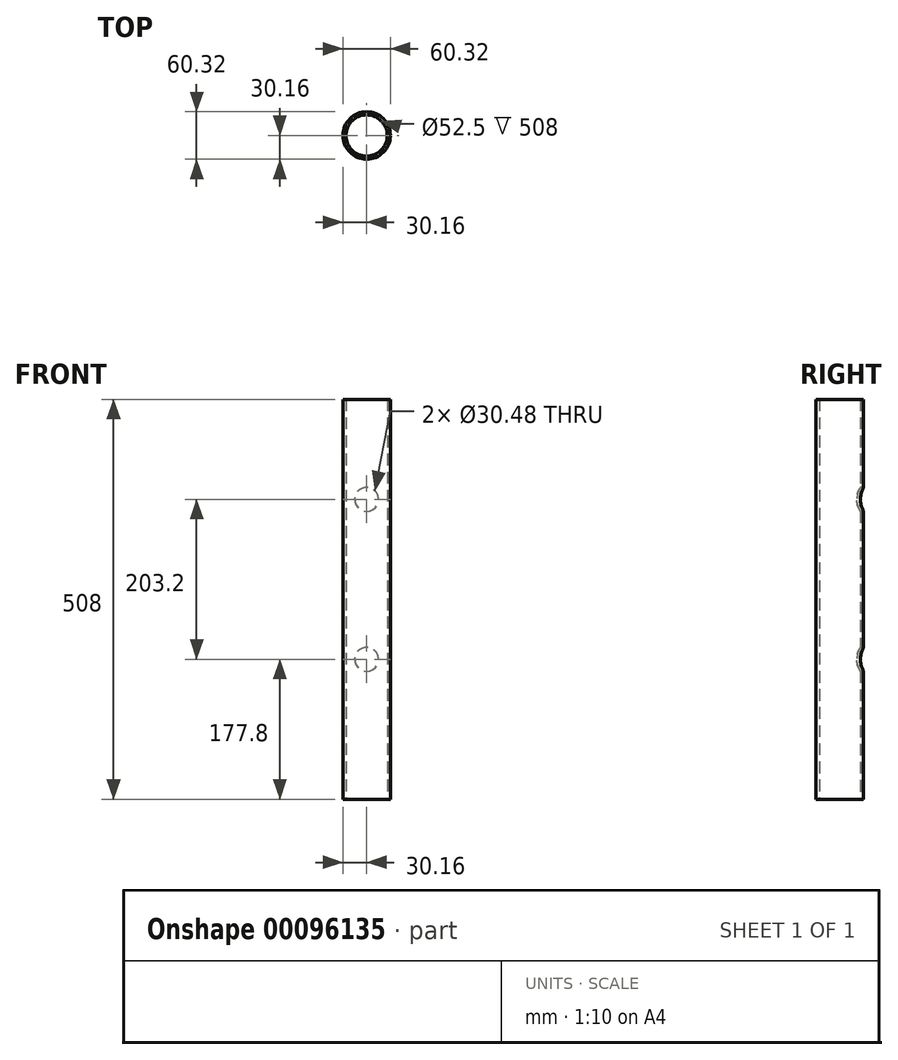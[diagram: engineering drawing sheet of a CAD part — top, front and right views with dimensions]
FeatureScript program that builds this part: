
annotation { "Feature Type Name" : "Feature", "Feature Type Description" : "" }
export const myFeature = defineFeature(function(context is Context, id is Id, definition is map)
    precondition{}
    {
        {
            var Q0;
            Q0=qCreatedBy(makeId("Top.planeOp"),FACE);
            var sketch = newSketch(context, id + "F0", { "sketchPlane" : qUnion([Q0])});
            skCircle(sketch, "E0", {"center": v(0, 0) * mm, "radius": 26.25 * mm});
            skCircle(sketch, "E1", {"center": v(0, 0) * mm, "radius": 30.16 * mm});
            skSolve(sketch);
        }
        {
            var Q0;
            Q0=makeQuery(id+"F0.imprint","IMPRINT",FACE,{"disambiguationData":[TD([[makeQuery(id+"F0.imprint","IMPRINT",EDGE,{"derivedFrom":sQuery(id+"F0.wireOp",EDGE,"E0")}),-1.0]])]});
            extrude(context, id + "F1", {"entities" : qUnion([Q0]), "depth" : 508 * mm});
        }
        {
            var Q0;
            Q0=qCreatedBy(makeId("Front.planeOp"),FACE);
            var sketch = newSketch(context, id + "F2", { "sketchPlane" : qUnion([Q0])});
            skCircle(sketch, "E2", {"center": v(0, 381) * mm, "radius": 15.24 * mm});
            skSolve(sketch);
        }
        {
            var Q0;
            Q0=qCreatedBy(makeId("Front.planeOp"),FACE);
            var sketch = newSketch(context, id + "F3", { "sketchPlane" : qUnion([Q0])});
            skCircle(sketch, "E3", {"center": v(0, 177.8) * mm, "radius": 15.24 * mm});
            skSolve(sketch);
        }
        {
            var Q0;
            Q0=qSketchRegion(id+"F2",true);
            extrude(context, id + "F4", {"entities" : qUnion([Q0]), "operationType" : NewBodyOperationType.REMOVE, "oppositeDirection" : true, "depth" : 106.83 * mm});
        }
        {
            var Q0;
            Q0=qSketchRegion(id+"F3",true);
            extrude(context, id + "F5", {"entities" : qUnion([Q0]), "operationType" : NewBodyOperationType.REMOVE, "oppositeDirection" : true, "depth" : 102.8 * mm});
        }
    });
